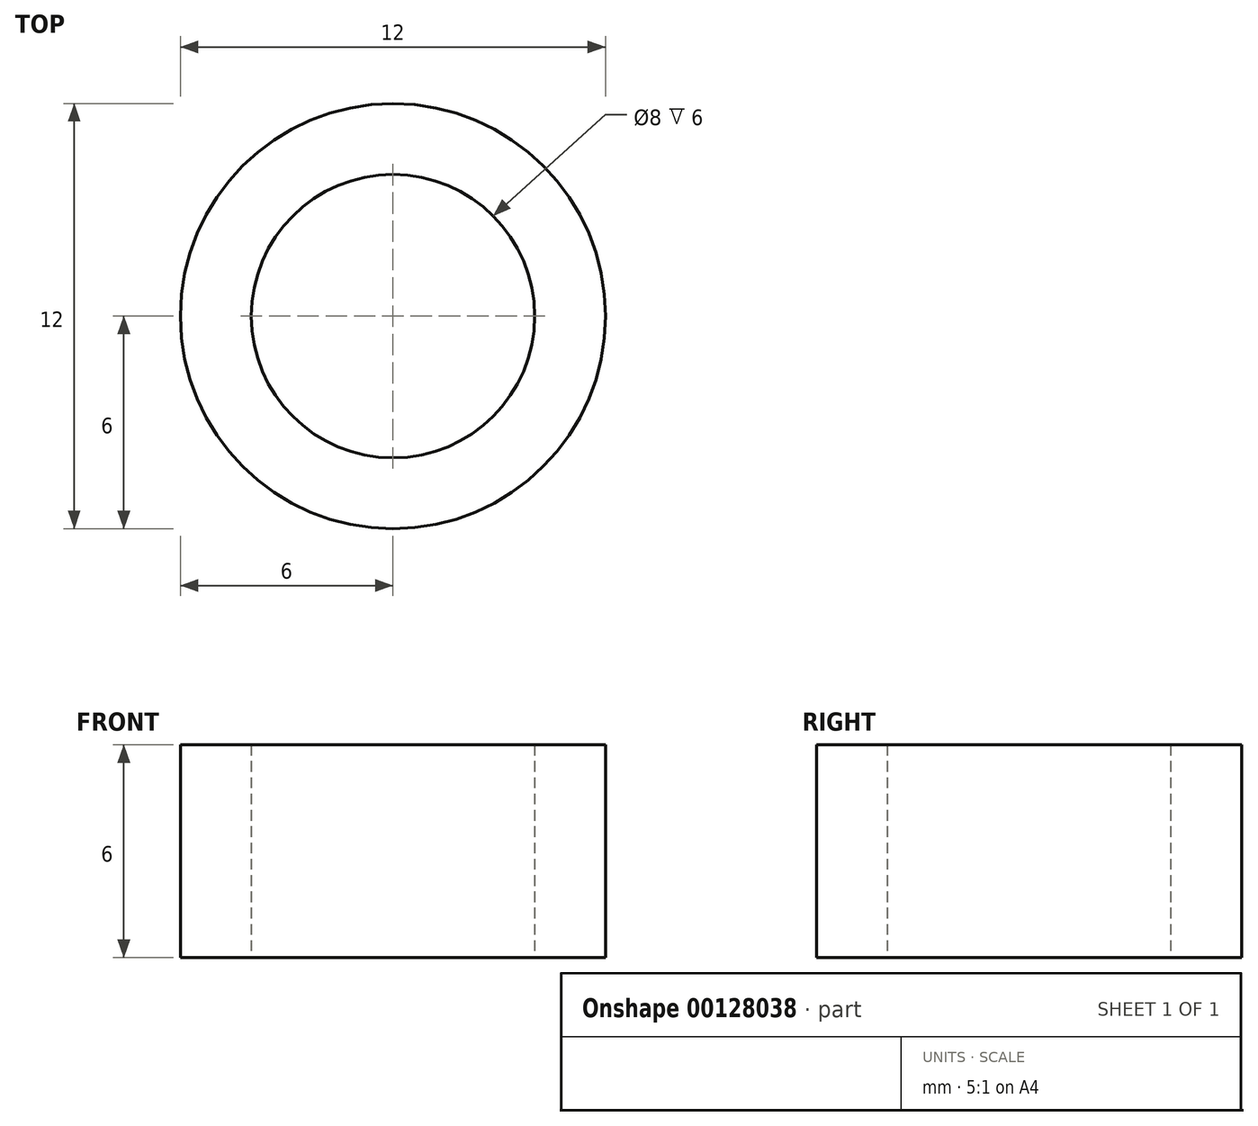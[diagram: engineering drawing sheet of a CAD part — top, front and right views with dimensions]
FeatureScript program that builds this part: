
annotation { "Feature Type Name" : "Feature", "Feature Type Description" : "" }
export const myFeature = defineFeature(function(context is Context, id is Id, definition is map)
    precondition{}
    {
        {
            var Q0;
            Q0=qCreatedBy(makeId("Top.planeOp"),FACE);
            var sketch = newSketch(context, id + "F0", { "sketchPlane" : qUnion([Q0])});
            skCircle(sketch, "E0", {"center": v(0, 0) * mm, "radius": 4 * mm});
            skCircle(sketch, "E1", {"center": v(0, 0) * mm, "radius": 6 * mm});
            skSolve(sketch);
        }
        {
            var Q0;
            Q0 = qSketchRegion(id + "F0", true);
            extrude(context, id + "F1", {"entities" : qUnion([Q0]), "depth" : 6 * mm});
        }
    });
